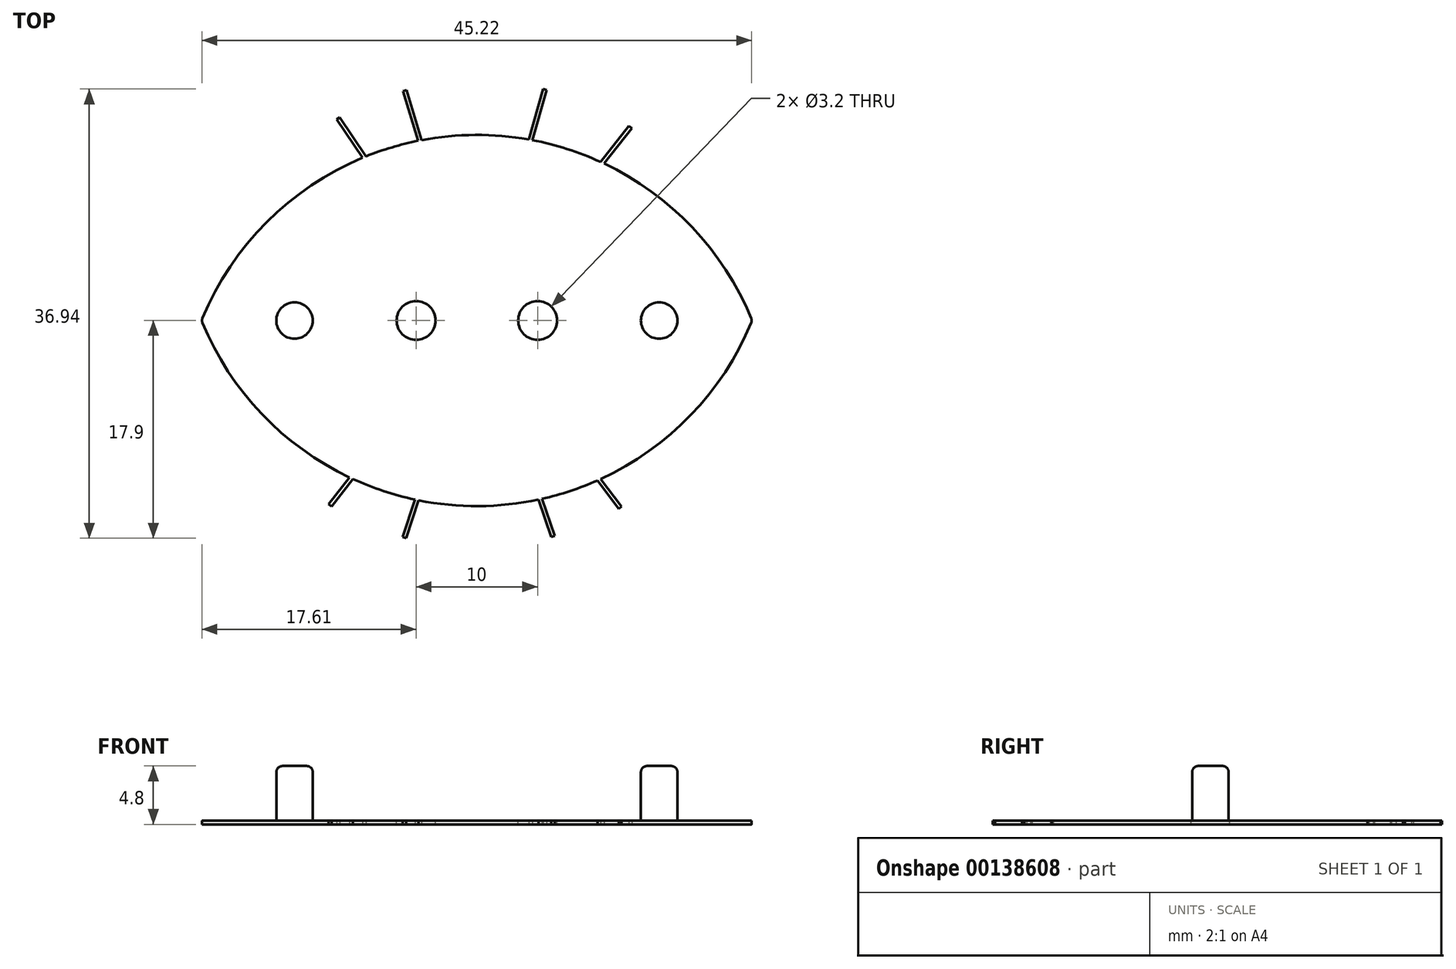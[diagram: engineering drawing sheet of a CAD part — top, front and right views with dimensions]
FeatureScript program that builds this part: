
annotation { "Feature Type Name" : "Feature", "Feature Type Description" : "" }
export const myFeature = defineFeature(function(context is Context, id is Id, definition is map)
    precondition{}
    {
        {
            assignVariable(context, id + "F0", {"name" : "pin_length", "anyValue" : 4.5 * mm});
        }
        {
            assignVariable(context, id + "F1", {"name" : "pin_end_fillet", "anyValue" : 0.5 * mm});
        }
        {
            var Q0;
            Q0=qCreatedBy(makeId("Top.planeOp"),FACE);
            var sketch = newSketch(context, id + "F2", { "sketchPlane" : qUnion([Q0])});
            skCircle(sketch, "E0", {"center": v(0, 0) * mm, "radius": 22 * mm, "construction": true});
            skLineSegment(sketch, "E1", {"start": v(-22, 0) * mm, "end": v(22, 0) * mm, "construction": true});
            skLineSegment(sketch, "E2", {"start": v(0, 22) * mm, "end": v(0, 14.67) * mm, "construction": true});
            skLineSegment(sketch, "E3", {"start": v(0, 14.67) * mm, "end": v(0, 7.33) * mm, "construction": true});
            skLineSegment(sketch, "E4", {"start": v(0, 7.33) * mm, "end": v(0, 0) * mm, "construction": true});
            skArc(sketch, "E5", {"start": v(21.93, 0.16) * mm, "mid": v(0, 14.67) * mm, "end": v(-21.93, 0.16) * mm, "construction": true});
            skArc(sketch, "E6.MirrorCS", {"start": v(21.93, -0.16) * mm, "mid": v(0, -14.67) * mm, "end": v(-21.93, -0.16) * mm, "construction": true});
            skPoint(sketch, "E7.visualSharp", {"position": v(22, 0) * mm});
            skArc(sketch, "E7.filletArc", {"start": v(21.93, -0.16) * mm, "mid": v(21.97, 0) * mm, "end": v(21.93, 0.16) * mm});
            skPoint(sketch, "E8.visualSharp", {"position": v(-22, 0) * mm});
            skArc(sketch, "E8.filletArc", {"start": v(-21.93, 0.16) * mm, "mid": v(-21.97, 0) * mm, "end": v(-21.93, -0.16) * mm});
            skArc(sketch, "E9.0", {"start": v(22.57, 0.2) * mm, "mid": v(17.7, 7.68) * mm, "end": v(10.47, 12.91) * mm});
            skArc(sketch, "E10.0", {"start": v(22.57, -0.2) * mm, "mid": v(17.6, -7.78) * mm, "end": v(10.2, -13.04) * mm});
            skPoint(sketch, "E11.visualSharp", {"position": v(-22.65, 0) * mm});
            skArc(sketch, "E11.filletArc", {"start": v(-22.57, 0.2) * mm, "mid": v(-22.6, 0) * mm, "end": v(-22.57, -0.2) * mm});
            skPoint(sketch, "E12.visualSharp", {"position": v(22.65, 0) * mm});
            skArc(sketch, "E12.filletArc", {"start": v(22.57, -0.2) * mm, "mid": v(22.6, 0) * mm, "end": v(22.57, 0.2) * mm});
            skLineSegment(sketch, "E13", {"start": v(4.27, 14.9) * mm, "end": v(5.46, 19.04) * mm});
            skLineSegment(sketch, "E14", {"start": v(-4.54, 14.84) * mm, "end": v(-5.8, 18.95) * mm});
            skLineSegment(sketch, "E15", {"start": v(-9.1, 13.5) * mm, "end": v(-11.27, 16.71) * mm});
            skArc(sketch, "E16", {"start": v(22.65, 0) * mm, "mid": v(0.12, 19.7) * mm, "end": v(-22.57, 0.2) * mm, "construction": true});
            skLineSegment(sketch, "E17", {"start": v(-11.52, 16.54) * mm, "end": v(-11.27, 16.71) * mm});
            skLineSegment(sketch, "E18", {"start": v(-6.08, 18.86) * mm, "end": v(-5.8, 18.95) * mm});
            skLineSegment(sketch, "E19", {"start": v(5.46, 19.04) * mm, "end": v(5.75, 18.96) * mm});
            skLineSegment(sketch, "E20", {"start": v(12.5, 16) * mm, "end": v(12.75, 15.83) * mm});
            skLineSegment(sketch, "E21.trimOffspring", {"start": v(10.47, 12.91) * mm, "end": v(12.75, 15.83) * mm});
            skLineSegment(sketch, "E22.trimOffspring", {"start": v(10.19, 13.04) * mm, "end": v(12.5, 16) * mm});
            skLineSegment(sketch, "E23.trimOffspring", {"start": v(4.57, 14.84) * mm, "end": v(5.75, 18.96) * mm});
            skLineSegment(sketch, "E24.trimOffspring", {"start": v(-4.83, 14.78) * mm, "end": v(-6.08, 18.86) * mm});
            skLineSegment(sketch, "E25.trimOffspring", {"start": v(-9.4, 13.39) * mm, "end": v(-11.52, 16.54) * mm});
            skArc(sketch, "E26.trimOffspring", {"start": v(10.19, 13.04) * mm, "mid": v(7.43, 14.1) * mm, "end": v(4.57, 14.84) * mm});
            skArc(sketch, "E27.trimOffspring", {"start": v(4.27, 14.9) * mm, "mid": v(-0.14, 15.27) * mm, "end": v(-4.54, 14.84) * mm});
            skArc(sketch, "E28.trimOffspring", {"start": v(-4.83, 14.78) * mm, "mid": v(-7, 14.24) * mm, "end": v(-9.1, 13.5) * mm});
            skArc(sketch, "E29.trimOffspring", {"start": v(-9.4, 13.39) * mm, "mid": v(-17.3, 8.1) * mm, "end": v(-22.57, 0.2) * mm});
            skArc(sketch, "E30", {"start": v(-22.65, 0) * mm, "mid": v(0, -18.64) * mm, "end": v(22.65, 0) * mm, "construction": true});
            skLineSegment(sketch, "E31", {"start": v(5.07, -14.73) * mm, "end": v(6.13, -17.81) * mm});
            skLineSegment(sketch, "E32", {"start": v(-4.8, -14.79) * mm, "end": v(-5.82, -17.9) * mm});
            skLineSegment(sketch, "E33", {"start": v(0, 0) * mm, "end": v(0, -15.27) * mm, "construction": true});
            skLineSegment(sketch, "E34", {"start": v(-12.2, -15.12) * mm, "end": v(-11.96, -15.3) * mm});
            skLineSegment(sketch, "E35", {"start": v(-6.1, -17.8) * mm, "end": v(-5.82, -17.9) * mm});
            skLineSegment(sketch, "E36", {"start": v(6.13, -17.81) * mm, "end": v(6.42, -17.72) * mm});
            skLineSegment(sketch, "E37", {"start": v(11.66, -15.48) * mm, "end": v(11.9, -15.3) * mm});
            skArc(sketch, "E38.trimOffspring", {"start": v(9.92, -13.16) * mm, "mid": v(7.68, -14.03) * mm, "end": v(5.37, -14.67) * mm});
            skLineSegment(sketch, "E39.trimOffspring", {"start": v(10.2, -13.04) * mm, "end": v(11.9, -15.3) * mm});
            skLineSegment(sketch, "E40.trimOffspring", {"start": v(9.92, -13.16) * mm, "end": v(11.66, -15.48) * mm});
            skLineSegment(sketch, "E41.trimOffspring", {"start": v(5.37, -14.67) * mm, "end": v(6.42, -17.72) * mm});
            skArc(sketch, "E42.trimOffspring", {"start": v(5.07, -14.73) * mm, "mid": v(0.14, -15.27) * mm, "end": v(-4.8, -14.79) * mm});
            skLineSegment(sketch, "E43.trimOffspring", {"start": v(-5.1, -14.73) * mm, "end": v(-6.1, -17.8) * mm});
            skArc(sketch, "E44.trimOffspring", {"start": v(-5.1, -14.73) * mm, "mid": v(-7.7, -14.02) * mm, "end": v(-10.19, -13.04) * mm});
            skArc(sketch, "E45.trimOffspring", {"start": v(-10.47, -12.91) * mm, "mid": v(-17.7, -7.68) * mm, "end": v(-22.57, -0.2) * mm});
            skLineSegment(sketch, "E46.trimOffspring", {"start": v(-10.47, -12.91) * mm, "end": v(-12.2, -15.12) * mm});
            skLineSegment(sketch, "E47.trimOffspring", {"start": v(-10.19, -13.04) * mm, "end": v(-11.96, -15.3) * mm});
            skSolve(sketch);
        }
        {
            var Q0;
            Q0=makeQuery(id+"F2.imprint","IMPRINT",FACE,{"disambiguationData":[TD([[makeQuery(id+"F2.imprint","IMPRINT",EDGE,{"derivedFrom":sQuery(id+"F2.wireOp",EDGE,"E5")}),1.0]])]});
            var Q1;
            Q1=makeQuery(id+"F2.imprint","IMPRINT",FACE,{"disambiguationData":[TD([[makeQuery(id+"F2.imprint","IMPRINT",EDGE,{"derivedFrom":sQuery(id+"F2.wireOp",EDGE,"E9.0")}),1.0]])]});
            extrude(context, id + "F3", {"entities" : qUnion([Q0, Q1]), "depth" : 0.3 * mm});
        }
        {
            var Q0;
            Q0=makeQuery(id+"F3.opExtrude","CAP_FACE",FACE,{"disambiguationData":[OSD([sQuery(id+"F2.wireOp",EDGE,"E9.0"),sQuery(id+"F2.wireOp",EDGE,"E10.0"),sQuery(id+"F2.wireOp",EDGE,"E11.filletArc"),sQuery(id+"F2.wireOp",EDGE,"E12.filletArc")])],"isStart":false});
            var sketch = newSketch(context, id + "F4", { "sketchPlane" : qUnion([Q0])});
            skLineSegment(sketch, "E48", {"start": v(0, 0) * mm, "end": v(5, 0) * mm, "construction": true});
            skLineSegment(sketch, "E49", {"start": v(0, 0) * mm, "end": v(-5, 0) * mm, "construction": true});
            skCircle(sketch, "E50", {"center": v(5, 0) * mm, "radius": 1.6 * mm});
            skCircle(sketch, "E51", {"center": v(-5, 0) * mm, "radius": 1.6 * mm});
            skSolve(sketch);
        }
        {
            var Q0;
            Q0 = qSketchRegion(id + "F4", true);
            extrude(context, id + "F5", {"entities" : qUnion([Q0]), "operationType" : NewBodyOperationType.REMOVE, "endBound" : BoundingType.THROUGH_ALL, "oppositeDirection" : true, "depth" : 25.4 * mm});
        }
        {
            var Q0;
            Q0=makeQuery(id+"F3.opExtrude","CAP_FACE",FACE,{"disambiguationData":[OSD([sQuery(id+"F2.wireOp",EDGE,"E9.0"),sQuery(id+"F2.wireOp",EDGE,"E10.0"),sQuery(id+"F2.wireOp",EDGE,"E11.filletArc"),sQuery(id+"F2.wireOp",EDGE,"E12.filletArc"),sQuery(id+"F2.wireOp",EDGE,"E13"),sQuery(id+"F2.wireOp",EDGE,"E14"),sQuery(id+"F2.wireOp",EDGE,"E15"),sQuery(id+"F2.wireOp",EDGE,"E17"),sQuery(id+"F2.wireOp",EDGE,"E18"),sQuery(id+"F2.wireOp",EDGE,"E19"),sQuery(id+"F2.wireOp",EDGE,"E20"),sQuery(id+"F2.wireOp",EDGE,"E21.trimOffspring"),sQuery(id+"F2.wireOp",EDGE,"E22.trimOffspring"),sQuery(id+"F2.wireOp",EDGE,"E23.trimOffspring"),sQuery(id+"F2.wireOp",EDGE,"E24.trimOffspring"),sQuery(id+"F2.wireOp",EDGE,"E25.trimOffspring"),sQuery(id+"F2.wireOp",EDGE,"E26.trimOffspring"),sQuery(id+"F2.wireOp",EDGE,"E27.trimOffspring"),sQuery(id+"F2.wireOp",EDGE,"E28.trimOffspring"),sQuery(id+"F2.wireOp",EDGE,"E29.trimOffspring"),sQuery(id+"F2.wireOp",EDGE,"E31"),sQuery(id+"F2.wireOp",EDGE,"E32"),sQuery(id+"F2.wireOp",EDGE,"E34"),sQuery(id+"F2.wireOp",EDGE,"E35"),sQuery(id+"F2.wireOp",EDGE,"E36"),sQuery(id+"F2.wireOp",EDGE,"E37"),sQuery(id+"F2.wireOp",EDGE,"E38.trimOffspring"),sQuery(id+"F2.wireOp",EDGE,"E39.trimOffspring"),sQuery(id+"F2.wireOp",EDGE,"E40.trimOffspring"),sQuery(id+"F2.wireOp",EDGE,"E41.trimOffspring"),sQuery(id+"F2.wireOp",EDGE,"E42.trimOffspring"),sQuery(id+"F2.wireOp",EDGE,"E43.trimOffspring"),sQuery(id+"F2.wireOp",EDGE,"E44.trimOffspring"),sQuery(id+"F2.wireOp",EDGE,"E45.trimOffspring"),sQuery(id+"F2.wireOp",EDGE,"E46.trimOffspring"),sQuery(id+"F2.wireOp",EDGE,"E47.trimOffspring")])],"isStart":false});
            var sketch = newSketch(context, id + "F6", { "sketchPlane" : qUnion([Q0])});
            skLineSegment(sketch, "E52", {"start": v(0, 0) * mm, "end": v(15, 0) * mm, "construction": true});
            skLineSegment(sketch, "E53", {"start": v(0, 0) * mm, "end": v(-15, 0) * mm, "construction": true});
            skCircle(sketch, "E54", {"center": v(15, 0) * mm, "radius": 1.5 * mm});
            skCircle(sketch, "E55", {"center": v(-15, 0) * mm, "radius": 1.5 * mm});
            skSolve(sketch);
        }
        {
            var Q0;
            Q0=makeQuery(id+"F6.imprint","IMPRINT",FACE,{"disambiguationData":[TD([[makeQuery(id+"F6.imprint","IMPRINT",EDGE,{"derivedFrom":sQuery(id+"F6.wireOp",EDGE,"E55")}),1.0]])]});
            var Q1;
            Q1=makeQuery(id+"F6.imprint","IMPRINT",FACE,{"disambiguationData":[TD([[makeQuery(id+"F6.imprint","IMPRINT",EDGE,{"derivedFrom":sQuery(id+"F6.wireOp",EDGE,"E54")}),1.0]])]});
            extrude(context, id + "F7", {"entities" : qUnion([Q0, Q1]), "operationType" : NewBodyOperationType.ADD, "depth" : getVariable(context, 'pin_length')});
        }
        {
            var Q0;
            Q0=makeQuery(id+"F7.opExtrude","CAP_EDGE",EDGE,{"disambiguationData":[OSD([sQuery(id+"F6.wireOp",EDGE,"E55")])],"isStart":false});
            var Q1;
            Q1=makeQuery(id+"F7.opExtrude","CAP_EDGE",EDGE,{"disambiguationData":[OSD([sQuery(id+"F6.wireOp",EDGE,"E54")])],"isStart":false});
            fillet(context, id + "F8", {"entities" : qUnion([Q0, Q1]), "radius" : getVariable(context, 'pin_end_fillet'), "tangentPropagation" : true, "allowEdgeOverflow" : false});
        }
    });
